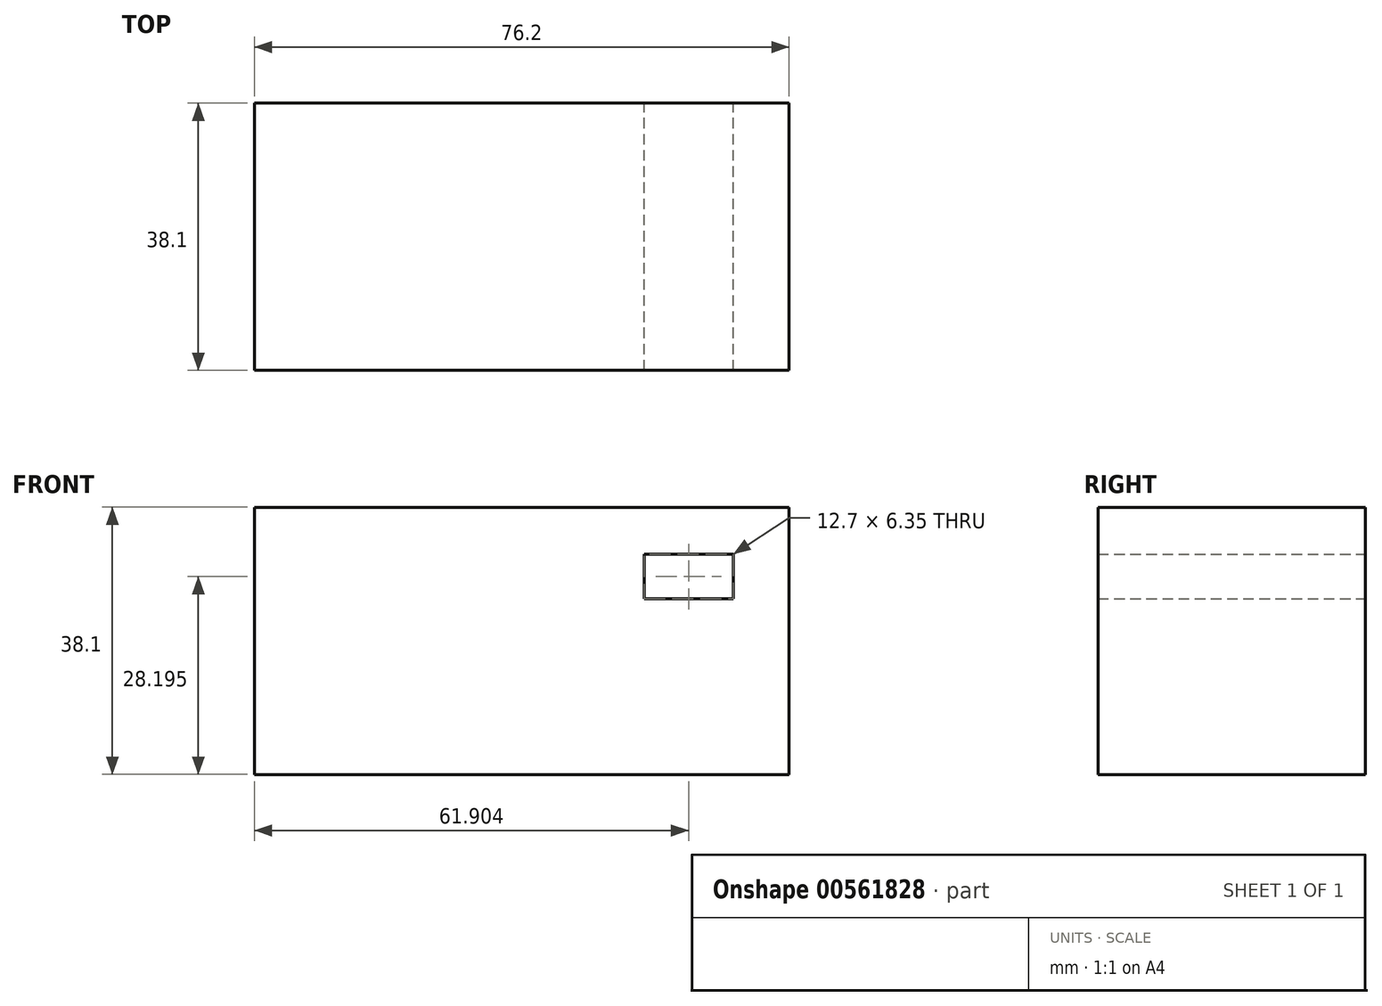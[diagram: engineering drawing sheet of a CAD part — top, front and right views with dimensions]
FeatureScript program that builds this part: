
annotation { "Feature Type Name" : "Feature", "Feature Type Description" : "" }
export const myFeature = defineFeature(function(context is Context, id is Id, definition is map)
    precondition{}
    {
        {
            var Q0;
            Q0=qCreatedBy(makeId("Front.planeOp"),FACE);
            var sketch = newSketch(context, id + "F0", { "sketchPlane" : qUnion([Q0])});
            skLineSegment(sketch, "E0.bottom", {"start": v(-64.4, 48.4) * mm, "end": v(11.8, 48.4) * mm});
            skLineSegment(sketch, "E0.top", {"start": v(-64.4, 10.3) * mm, "end": v(11.8, 10.3) * mm});
            skLineSegment(sketch, "E0.left", {"start": v(-64.4, 48.4) * mm, "end": v(-64.4, 10.3) * mm});
            skLineSegment(sketch, "E0.right", {"start": v(11.8, 48.4) * mm, "end": v(11.8, 10.3) * mm});
            skLineSegment(sketch, "E1.bottom", {"start": v(-8.86, 41.67) * mm, "end": v(3.84, 41.67) * mm});
            skLineSegment(sketch, "E1.top", {"start": v(-8.86, 35.32) * mm, "end": v(3.84, 35.32) * mm});
            skLineSegment(sketch, "E1.left", {"start": v(-8.86, 41.67) * mm, "end": v(-8.86, 35.32) * mm});
            skLineSegment(sketch, "E1.right", {"start": v(3.84, 41.67) * mm, "end": v(3.84, 35.32) * mm});
            skSolve(sketch);
        }
        {
            var Q0;
            Q0 = qSketchRegion(id + "F0", true);
            var Q1;
            Q1=makeQuery(id+"F0.imprint","IMPRINT",FACE,{"disambiguationData":[TD([[makeQuery(id+"F0.imprint","IMPRINT",EDGE,{"derivedFrom":sQuery(id+"F0.wireOp",EDGE,"E0.bottom")}),-1.0]])]});
            extrude(context, id + "F1", {"entities" : qUnion([Q0, Q1]), "depth" : 38.1 * mm, "offsetDistance" : 25.4 * mm});
        }
    });
